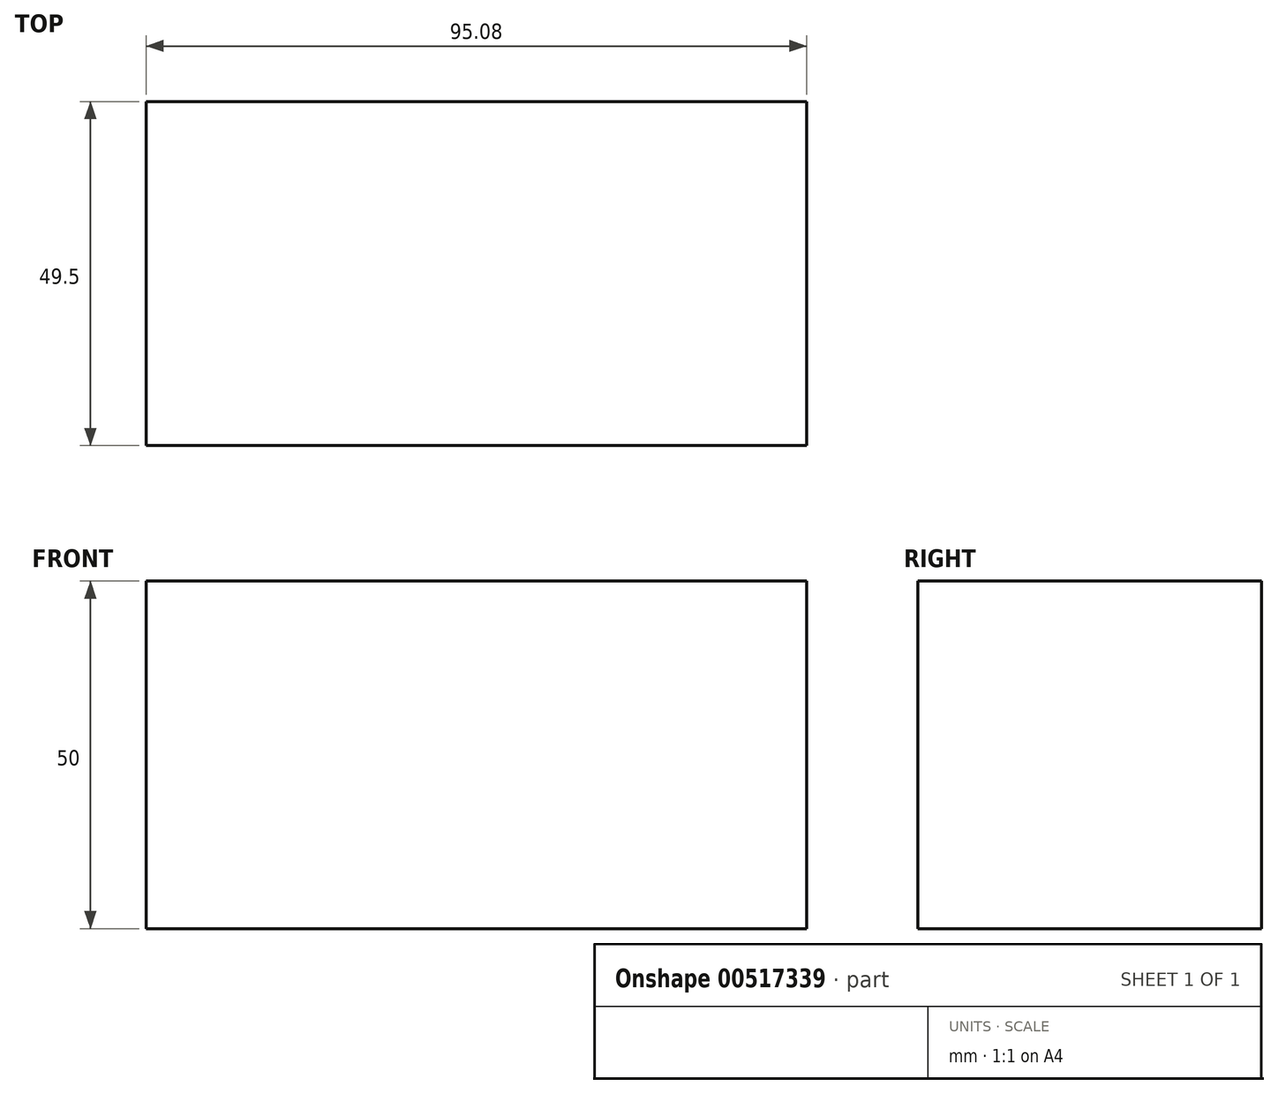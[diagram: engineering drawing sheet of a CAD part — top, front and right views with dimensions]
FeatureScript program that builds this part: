
annotation { "Feature Type Name" : "Feature", "Feature Type Description" : "" }
export const myFeature = defineFeature(function(context is Context, id is Id, definition is map)
    precondition{}
    {
        {
            var Q0;
            Q0=qCreatedBy(makeId("Top.planeOp"),FACE);
            var sketch = newSketch(context, id + "F0", { "sketchPlane" : qUnion([Q0])});
            skLineSegment(sketch, "E0.bottom", {"start": v(-47.05, 22.67) * mm, "end": v(48.03, 22.67) * mm});
            skLineSegment(sketch, "E0.top", {"start": v(-47.05, -26.83) * mm, "end": v(48.03, -26.83) * mm});
            skLineSegment(sketch, "E0.left", {"start": v(-47.05, 22.67) * mm, "end": v(-47.05, -26.83) * mm});
            skLineSegment(sketch, "E0.right", {"start": v(48.03, 22.67) * mm, "end": v(48.03, -26.83) * mm});
            skSolve(sketch);
        }
        {
            var Q0;
            Q0=makeQuery(id+"F0.imprint","IMPRINT",FACE,{"disambiguationData":[TD([[makeQuery(id+"F0.imprint","IMPRINT",EDGE,{"derivedFrom":sQuery(id+"F0.wireOp",EDGE,"E0.bottom")}),-1.0]])]});
            extrude(context, id + "F1", {"entities" : qUnion([Q0]), "depth" : 50 * mm, "offsetDistance" : 25.4 * mm});
        }
        {
            var Q0;
            Q0=makeQuery(id+"F1.opExtrude","SWEPT_FACE",FACE,{"disambiguationData":[OSD([sQuery(id+"F0.wireOp",EDGE,"E0.left")])]});
            var sketch = newSketch(context, id + "F2", { "sketchPlane" : qUnion([Q0])});
            skLineSegment(sketch, "E1", {"start": v(0, 50) * mm, "end": v(0, 71.8) * mm});
            skPoint(sketch, "E1.startSnap0", {"position": v(2.08, 50) * mm});
            skLineSegment(sketch, "E2", {"start": v(0, 71.8) * mm, "end": v(-26.34, 50) * mm});
            skLineSegment(sketch, "E3.MirrorCS", {"start": v(0, 71.8) * mm, "end": v(26.34, 50) * mm});
            skSolve(sketch);
        }
        {
            var Q0;
            Q0=sQuery(id+"F2.wireOp",EDGE,"E2");
            var Q1;
            Q1=sQuery(id+"F2.wireOp",EDGE,"E3.MirrorCS");
            extrude(context, id + "F3", {"bodyType" : ToolBodyType.SURFACE, "surfaceEntities" : qUnion([Q0, Q1]), "depth" : -100 * mm, "offsetDistance" : 25.4 * mm});
        }
    });
